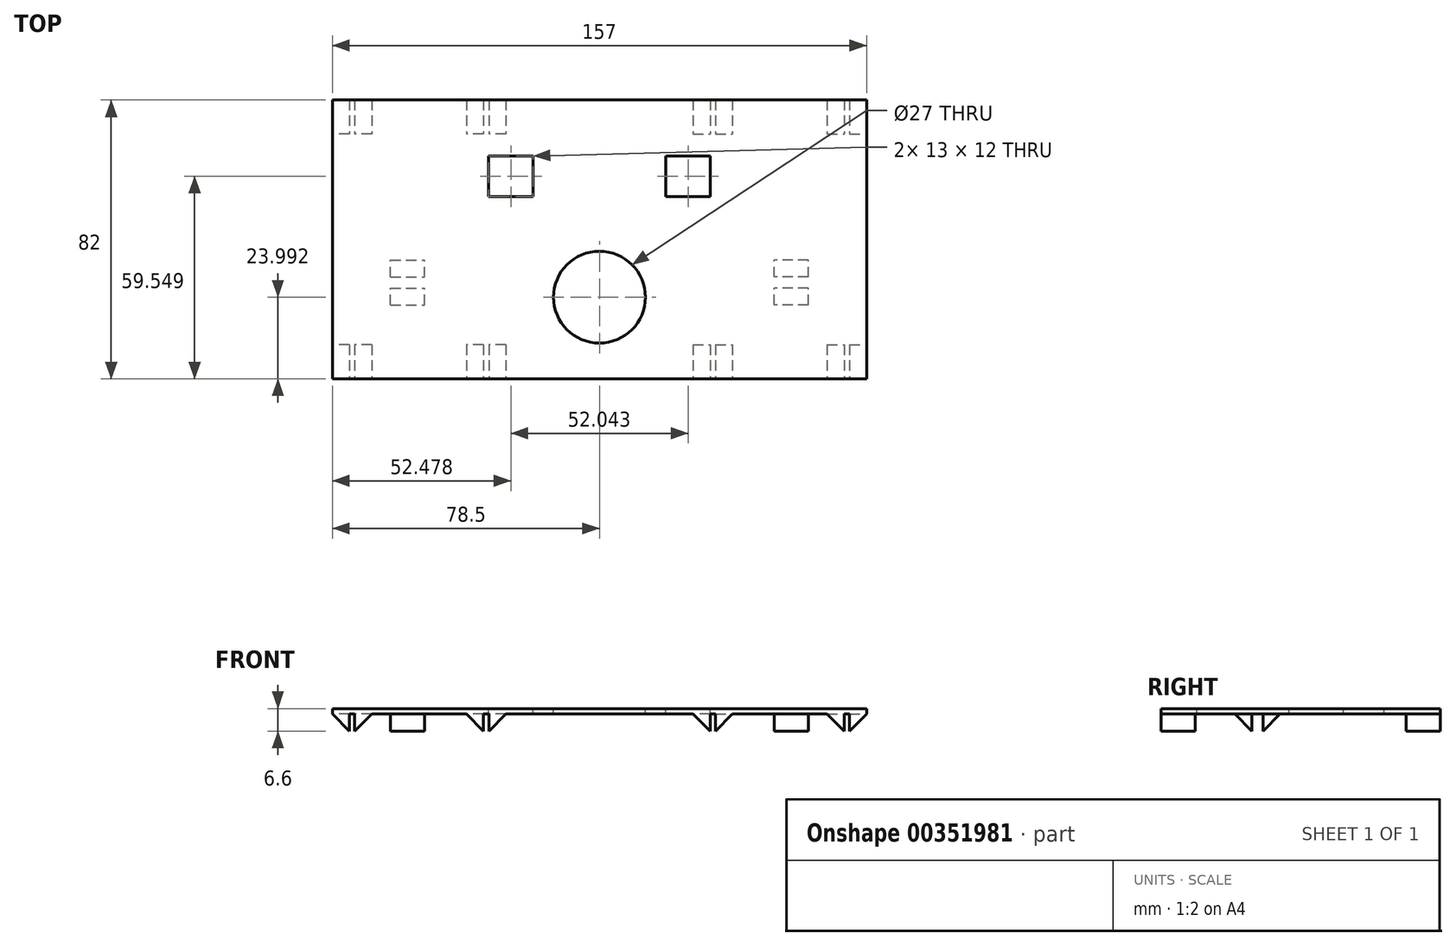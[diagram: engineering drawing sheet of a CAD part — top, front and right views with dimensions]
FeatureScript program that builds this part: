
annotation { "Feature Type Name" : "Feature", "Feature Type Description" : "" }
export const myFeature = defineFeature(function(context is Context, id is Id, definition is map)
    precondition{}
    {
        {
            var Q0;
            Q0=qCreatedBy(makeId("Front.planeOp"),FACE);
            cPlane(context, id + "F0", {"entities" : qUnion([Q0]), "cplaneType" : CPlaneType.OFFSET, "offset" : 41 * mm, "width" : 150 * mm, "height" : 150 * mm});
        }
        {
            var Q0;
            Q0=qCreatedBy(id+"F0.planeOp",FACE);
            var sketch = newSketch(context, id + "F1", { "sketchPlane" : qUnion([Q0])});
            skLineSegment(sketch, "E0", {"start": v(78.5, 1.6) * mm, "end": v(78.5, 0) * mm});
            skLineSegment(sketch, "E1", {"start": v(78.5, 0) * mm, "end": v(-78.5, 0) * mm});
            skLineSegment(sketch, "E2", {"start": v(-78.5, 0) * mm, "end": v(-78.5, 1.6) * mm});
            skLineSegment(sketch, "E3", {"start": v(-78.5, 1.6) * mm, "end": v(78.5, 1.6) * mm});
            skLineSegment(sketch, "E4", {"start": v(-73.5, -5) * mm, "end": v(-73.5, 0) * mm});
            skLineSegment(sketch, "E5", {"start": v(-78.5, 0) * mm, "end": v(-73.5, 0) * mm});
            skLineSegment(sketch, "E6", {"start": v(-71.9, 0) * mm, "end": v(-71.9, -5) * mm});
            skLineSegment(sketch, "E7", {"start": v(-66.9, 0) * mm, "end": v(-71.9, 0) * mm});
            skLineSegment(sketch, "E8", {"start": v(-32.5, 0) * mm, "end": v(-32.5, -5) * mm});
            skLineSegment(sketch, "E9", {"start": v(-27.5, 0) * mm, "end": v(-32.5, 0) * mm});
            skLineSegment(sketch, "E10", {"start": v(-34.1, 0) * mm, "end": v(-34.1, -5) * mm});
            skLineSegment(sketch, "E11", {"start": v(-39.1, 0) * mm, "end": v(-34.1, 0) * mm});
            skLineSegment(sketch, "E12.MirrorCS", {"start": v(27.5, -10) * mm, "end": v(27.5, 0) * mm});
            skLineSegment(sketch, "E13.MirrorCS", {"start": v(32.5, 0) * mm, "end": v(32.5, -5) * mm});
            skLineSegment(sketch, "E14.MirrorCS", {"start": v(39.1, -10) * mm, "end": v(39.1, 0) * mm});
            skLineSegment(sketch, "E15.MirrorCS", {"start": v(34.1, 0) * mm, "end": v(34.1, -5) * mm});
            skLineSegment(sketch, "E16.MirrorCS", {"start": v(34.1, -5) * mm, "end": v(35.7, -5) * mm});
            skLineSegment(sketch, "E17.MirrorCS", {"start": v(39.1, 0) * mm, "end": v(34.1, 0) * mm});
            skLineSegment(sketch, "E18.MirrorCS", {"start": v(71.9, 0) * mm, "end": v(71.9, -5) * mm});
            skLineSegment(sketch, "E19.MirrorCS", {"start": v(66.9, -10) * mm, "end": v(66.9, 0) * mm});
            skLineSegment(sketch, "E20.MirrorCS", {"start": v(66.9, 0) * mm, "end": v(71.9, 0) * mm});
            skLineSegment(sketch, "E21.MirrorCS", {"start": v(73.5, -5) * mm, "end": v(73.5, 0) * mm});
            skLineSegment(sketch, "E22.MirrorCS", {"start": v(78.5, 0) * mm, "end": v(73.5, 0) * mm});
            skLineSegment(sketch, "E23.MirrorCS", {"start": v(78.5, 0) * mm, "end": v(78.5, -10) * mm});
            skLineSegment(sketch, "E24.MirrorCS", {"start": v(75.1, -5) * mm, "end": v(73.5, -5) * mm});
            skLineSegment(sketch, "E25.MirrorCS", {"start": v(71.9, -5) * mm, "end": v(70.3, -5) * mm});
            skLineSegment(sketch, "E26.MirrorCS", {"start": v(32.5, -5) * mm, "end": v(30.9, -5) * mm});
            skLineSegment(sketch, "E27", {"start": v(-32.5, 0) * mm, "end": v(-27.5, 0) * mm});
            skLineSegment(sketch, "E28", {"start": v(27.5, 0) * mm, "end": v(32.5, 0) * mm});
            skLineSegment(sketch, "E29", {"start": v(-73.5, -5) * mm, "end": v(-78.5, 0) * mm});
            skLineSegment(sketch, "E30", {"start": v(-66.9, 0) * mm, "end": v(-71.9, -5) * mm});
            skLineSegment(sketch, "E31", {"start": v(-39.1, 0) * mm, "end": v(-34.1, -5) * mm});
            skLineSegment(sketch, "E32", {"start": v(-27.5, 0) * mm, "end": v(-32.5, -5) * mm});
            skSolve(sketch);
        }
        {
            var Q0;
            Q0=makeQuery(id+"F1.imprint","IMPRINT",FACE,{"disambiguationData":[TD([[makeQuery(id+"F1.imprint","IMPRINT",EDGE,{"derivedFrom":sQuery(id+"F1.wireOp",EDGE,"E0")}),-1.0]])]});
            extrude(context, id + "F2", {"entities" : qUnion([Q0]), "oppositeDirection" : true, "depth" : 82 * mm});
        }
        {
            var Q0;
            Q0=makeQuery(id+"F1.imprint","IMPRINT",FACE,{"disambiguationData":[TD([[makeQuery(id+"F1.imprint","IMPRINT",EDGE,{"derivedFrom":sQuery(id+"F1.wireOp",EDGE,"FF6IQarz-4mcM-jOca-ocC3-CsUcrpMwuvCt")}),1.0]])]});
            var Q1;
            Q1=makeQuery(id+"F1.imprint","IMPRINT",FACE,{"disambiguationData":[TD([[makeQuery(id+"F1.imprint","IMPRINT",EDGE,{"derivedFrom":sQuery(id+"F1.wireOp",EDGE,"E6")}),1.0]])]});
            var Q2;
            Q2=makeQuery(id+"F1.imprint","IMPRINT",FACE,{"disambiguationData":[TD([[makeQuery(id+"F1.imprint","IMPRINT",EDGE,{"derivedFrom":sQuery(id+"F1.wireOp",EDGE,"E10")}),-1.0]])]});
            var Q3;
            Q3=makeQuery(id+"F1.imprint","IMPRINT",FACE,{"disambiguationData":[TD([[makeQuery(id+"F1.imprint","IMPRINT",EDGE,{"derivedFrom":sQuery(id+"F1.wireOp",EDGE,"E8")}),1.0]])]});
            var Q4;
            Q4=makeQuery(id+"F1.imprint","IMPRINT",FACE,{"disambiguationData":[TD([[makeQuery(id+"F1.imprint","IMPRINT",EDGE,{"derivedFrom":sQuery(id+"F1.wireOp",EDGE,"E12.MirrorCS")}),-1.0]])]});
            var Q5;
            Q5=makeQuery(id+"F1.imprint","IMPRINT",FACE,{"disambiguationData":[TD([[makeQuery(id+"F1.imprint","IMPRINT",EDGE,{"derivedFrom":sQuery(id+"F1.wireOp",EDGE,"E14.MirrorCS")}),1.0]])]});
            var Q6;
            Q6=makeQuery(id+"F1.imprint","IMPRINT",FACE,{"disambiguationData":[TD([[makeQuery(id+"F1.imprint","IMPRINT",EDGE,{"derivedFrom":sQuery(id+"F1.wireOp",EDGE,"E18.MirrorCS")}),-1.0]])]});
            var Q7;
            Q7=makeQuery(id+"F1.imprint","IMPRINT",FACE,{"disambiguationData":[TD([[makeQuery(id+"F1.imprint","IMPRINT",EDGE,{"derivedFrom":sQuery(id+"F1.wireOp",EDGE,"E21.MirrorCS")}),-1.0]])]});
            var Q8;
            Q8=makeQuery(id+"F1.imprint","IMPRINT",FACE,{"disambiguationData":[TD([[makeQuery(id+"F1.imprint","IMPRINT",EDGE,{"derivedFrom":sQuery(id+"F1.wireOp",EDGE,"E4")}),1.0]])]});
            extrude(context, id + "F3", {"entities" : qUnion([Q0, Q1, Q2, Q3, Q4, Q5, Q6, Q7, Q8]), "operationType" : NewBodyOperationType.ADD, "oppositeDirection" : true, "depth" : 10 * mm});
        }
        {
            var Q0;
            Q0=makeQuery(id+"F1.imprint","IMPRINT",FACE,{"disambiguationData":[TD([[makeQuery(id+"F1.imprint","IMPRINT",EDGE,{"derivedFrom":sQuery(id+"F1.wireOp",EDGE,"FF6IQarz-4mcM-jOca-ocC3-CsUcrpMwuvCt")}),1.0]])]});
            var Q1;
            Q1=makeQuery(id+"F1.imprint","IMPRINT",FACE,{"disambiguationData":[TD([[makeQuery(id+"F1.imprint","IMPRINT",EDGE,{"derivedFrom":sQuery(id+"F1.wireOp",EDGE,"E6")}),1.0]])]});
            var Q2;
            Q2=makeQuery(id+"F1.imprint","IMPRINT",FACE,{"disambiguationData":[TD([[makeQuery(id+"F1.imprint","IMPRINT",EDGE,{"derivedFrom":sQuery(id+"F1.wireOp",EDGE,"E10")}),-1.0]])]});
            var Q3;
            Q3=makeQuery(id+"F1.imprint","IMPRINT",FACE,{"disambiguationData":[TD([[makeQuery(id+"F1.imprint","IMPRINT",EDGE,{"derivedFrom":sQuery(id+"F1.wireOp",EDGE,"E8")}),1.0]])]});
            var Q4;
            Q4=makeQuery(id+"F1.imprint","IMPRINT",FACE,{"disambiguationData":[TD([[makeQuery(id+"F1.imprint","IMPRINT",EDGE,{"derivedFrom":sQuery(id+"F1.wireOp",EDGE,"E14.MirrorCS")}),1.0]])]});
            var Q5;
            Q5=makeQuery(id+"F1.imprint","IMPRINT",FACE,{"disambiguationData":[TD([[makeQuery(id+"F1.imprint","IMPRINT",EDGE,{"derivedFrom":sQuery(id+"F1.wireOp",EDGE,"E12.MirrorCS")}),-1.0]])]});
            var Q6;
            Q6=makeQuery(id+"F1.imprint","IMPRINT",FACE,{"disambiguationData":[TD([[makeQuery(id+"F1.imprint","IMPRINT",EDGE,{"derivedFrom":sQuery(id+"F1.wireOp",EDGE,"E18.MirrorCS")}),-1.0]])]});
            var Q7;
            Q7=makeQuery(id+"F1.imprint","IMPRINT",FACE,{"disambiguationData":[TD([[makeQuery(id+"F1.imprint","IMPRINT",EDGE,{"derivedFrom":sQuery(id+"F1.wireOp",EDGE,"E21.MirrorCS")}),-1.0]])]});
            var Q8;
            Q8=makeQuery(id+"F1.imprint","IMPRINT",FACE,{"disambiguationData":[TD([[makeQuery(id+"F1.imprint","IMPRINT",EDGE,{"derivedFrom":sQuery(id+"F1.wireOp",EDGE,"E4")}),1.0]])]});
            extrude(context, id + "F4", {"entities" : qUnion([Q0, Q1, Q2, Q3, Q4, Q5, Q6, Q7, Q8]), "operationType" : NewBodyOperationType.ADD, "oppositeDirection" : true, "depth" : 82 * mm, "hasSecondDirection" : true, "secondDirectionOppositeDirection" : true, "secondDirectionDepth" : 72 * mm});
        }
        {
            var Q0;
            Q0=qCreatedBy(makeId("Right.planeOp"),FACE);
            cPlane(context, id + "F5", {"entities" : qUnion([Q0]), "cplaneType" : CPlaneType.OFFSET, "offset" : 51.4 * mm, "oppositeDirection" : true, "width" : 150 * mm, "height" : 150 * mm});
        }
        {
            var Q0;
            Q0=qCreatedBy(id+"F5.planeOp",FACE);
            var sketch = newSketch(context, id + "F6", { "sketchPlane" : qUnion([Q0])});
            skLineSegment(sketch, "E33", {"start": v(-11.1, -5) * mm, "end": v(-11.1, 0) * mm});
            skLineSegment(sketch, "E34", {"start": v(-11.1, 0) * mm, "end": v(-6.1, 0) * mm});
            skLineSegment(sketch, "E35", {"start": v(-14.3, 0) * mm, "end": v(-14.3, -5) * mm});
            skLineSegment(sketch, "E36", {"start": v(-19.3, 0) * mm, "end": v(-14.3, 0) * mm});
            skLineSegment(sketch, "E37", {"start": v(-19.3, 0) * mm, "end": v(-14.3, -5) * mm});
            skLineSegment(sketch, "E38", {"start": v(-6.1, 0) * mm, "end": v(-11.1, -5) * mm});
            skSolve(sketch);
        }
        {
            var Q0;
            Q0=qSketchRegion(id+"F6",true);
            extrude(context, id + "F7", {"entities" : qUnion([Q0]), "operationType" : NewBodyOperationType.ADD, "oppositeDirection" : true, "depth" : 10 * mm});
        }
        {
            var Q0;
            Q0=qSketchRegion(id+"F6",true);
            extrude(context, id + "F8", {"entities" : qUnion([Q0]), "operationType" : NewBodyOperationType.ADD, "depth" : 112.8 * mm, "hasSecondDirection" : true, "secondDirectionOppositeDirection" : false, "secondDirectionDepth" : 102.8 * mm});
        }
        {
            var Q0;
            Q0=makeQuery(id+"F2.opExtrude","SWEPT_BODY",BODY,{"disambiguationData":[OSD([sQuery(id+"F1.wireOp",EDGE,"E0"),sQuery(id+"F1.wireOp",EDGE,"E1"),sQuery(id+"F1.wireOp",EDGE,"E2"),sQuery(id+"F1.wireOp",EDGE,"E3"),sQuery(id+"F1.wireOp",EDGE,"E5"),sQuery(id+"F1.wireOp",EDGE,"E7"),sQuery(id+"F1.wireOp",EDGE,"E11"),sQuery(id+"F1.wireOp",EDGE,"E17.MirrorCS"),sQuery(id+"F1.wireOp",EDGE,"E20.MirrorCS"),sQuery(id+"F1.wireOp",EDGE,"E22.MirrorCS"),sQuery(id+"F1.wireOp",EDGE,"E27"),sQuery(id+"F1.wireOp",EDGE,"E28")])]});
            var Q1;
            Q1=qCreatedBy(makeId("Right.planeOp"),FACE);
            mirror(context, id + "F9", {"operationType" : NewBodyOperationType.ADD, "entities" : qUnion([Q0]), "mirrorPlane" : qUnion([Q1])});
        }
        {
            var Q0;
            Q0=makeQuery(id+"F2.opExtrude","SWEPT_FACE",FACE,{"disambiguationData":[OSD([sQuery(id+"F1.wireOp",EDGE,"E3")])]});
            var sketch = newSketch(context, id + "F10", { "sketchPlane" : qUnion([Q0])});
            skCircle(sketch, "E39", {"center": v(0, -17) * mm, "radius": 13.5 * mm});
            skSolve(sketch);
        }
        {
            var Q0;
            Q0 = qSketchRegion(id + "F10", true);
            extrude(context, id + "F11", {"entities" : qUnion([Q0]), "operationType" : NewBodyOperationType.REMOVE, "oppositeDirection" : true, "depth" : 1.6 * mm});
        }
        {
            var Q0;
            Q0=makeQuery(id+"F2.opExtrude","SWEPT_FACE",FACE,{"disambiguationData":[OSD([sQuery(id+"F1.wireOp",EDGE,"E3")])]});
            var sketch = newSketch(context, id + "F12", { "sketchPlane" : qUnion([Q0])});
            skLineSegment(sketch, "E40.bottom", {"start": v(-32.52, 24.55) * mm, "end": v(-19.52, 24.55) * mm});
            skLineSegment(sketch, "E40.top", {"start": v(-32.52, 12.55) * mm, "end": v(-19.52, 12.55) * mm});
            skLineSegment(sketch, "E40.left", {"start": v(-32.52, 24.55) * mm, "end": v(-32.52, 12.55) * mm});
            skLineSegment(sketch, "E40.right", {"start": v(-19.52, 24.55) * mm, "end": v(-19.52, 12.55) * mm});
            skLineSegment(sketch, "E41.MirrorCS", {"start": v(32.52, 24.55) * mm, "end": v(19.52, 24.55) * mm});
            skLineSegment(sketch, "E42.MirrorCS", {"start": v(19.52, 24.55) * mm, "end": v(19.52, 12.55) * mm});
            skLineSegment(sketch, "E43.MirrorCS", {"start": v(32.52, 12.55) * mm, "end": v(19.52, 12.55) * mm});
            skLineSegment(sketch, "E44.MirrorCS", {"start": v(32.52, 24.55) * mm, "end": v(32.52, 12.55) * mm});
            skSolve(sketch);
        }
        {
            var Q0;
            Q0 = qSketchRegion(id + "F12", true);
            extrude(context, id + "F13", {"entities" : qUnion([Q0]), "operationType" : NewBodyOperationType.REMOVE, "oppositeDirection" : true, "depth" : 1.6 * mm});
        }
    });
